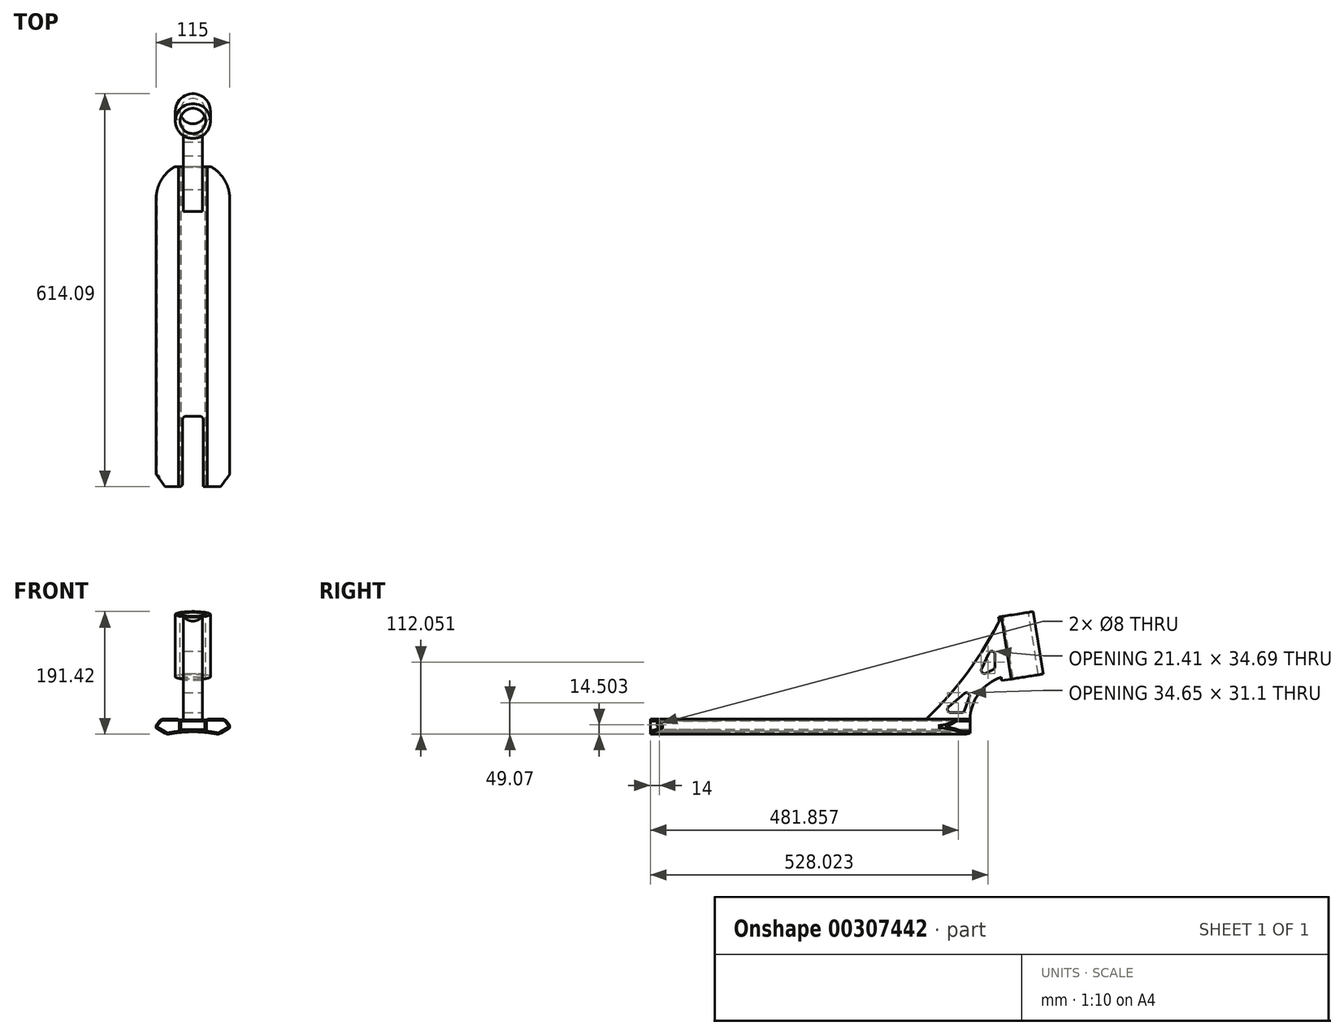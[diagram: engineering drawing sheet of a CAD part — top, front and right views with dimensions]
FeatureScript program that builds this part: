
annotation { "Feature Type Name" : "Feature", "Feature Type Description" : "" }
export const myFeature = defineFeature(function(context is Context, id is Id, definition is map)
    precondition{}
    {
        {
            var Q0;
            Q0=qCreatedBy(makeId("Front.planeOp"),FACE);
            var sketch = newSketch(context, id + "F0", { "sketchPlane" : qUnion([Q0])});
            skLineSegment(sketch, "E0", {"start": v(0, 0) * mm, "end": v(22.5, 0) * mm});
            skLineSegment(sketch, "E1", {"start": v(22.5, 0) * mm, "end": v(22.5, 1.3) * mm});
            skLineSegment(sketch, "E2", {"start": v(22.5, 1.3) * mm, "end": v(50.06, 1.3) * mm});
            skLineSegment(sketch, "E3", {"start": v(50.06, 1.3) * mm, "end": v(57.5, -8.7) * mm});
            skLineSegment(sketch, "E4", {"start": v(57.5, -8.7) * mm, "end": v(57.5, -12.7) * mm});
            skLineSegment(sketch, "E5", {"start": v(57.5, -12.7) * mm, "end": v(40.18, -22.7) * mm});
            skLineSegment(sketch, "E6.MirrorCS", {"start": v(0, 0) * mm, "end": v(-22.5, 0) * mm});
            skLineSegment(sketch, "E7.MirrorCS", {"start": v(-22.5, 0) * mm, "end": v(-22.5, 1.3) * mm});
            skLineSegment(sketch, "E8.MirrorCS", {"start": v(-22.5, 1.3) * mm, "end": v(-50.06, 1.3) * mm});
            skLineSegment(sketch, "E9.MirrorCS", {"start": v(-50.06, 1.3) * mm, "end": v(-57.5, -8.7) * mm});
            skLineSegment(sketch, "E10.MirrorCS", {"start": v(-57.5, -8.7) * mm, "end": v(-57.5, -12.7) * mm});
            skLineSegment(sketch, "E11.MirrorCS", {"start": v(-57.5, -12.7) * mm, "end": v(-40.18, -22.7) * mm});
            skArc(sketch, "E12", {"start": v(40.18, -22.7) * mm, "mid": v(0, -18.62) * mm, "end": v(-40.18, -22.7) * mm});
            skSolve(sketch);
        }
        {
            var Q0;
            Q0 = qSketchRegion(id + "F0", true);
            extrude(context, id + "F1", {"entities" : qUnion([Q0]), "endBound" : BoundingType.SYMMETRIC, "depth" : 500 * mm});
        }
        {
            var Q0;
            Q0=qCreatedBy(makeId("Front.planeOp"),FACE);
            var sketch = newSketch(context, id + "F2", { "sketchPlane" : qUnion([Q0])});
            skLineSegment(sketch, "E13.bottom", {"start": v(-19, -2) * mm, "end": v(19, -2) * mm});
            skLineSegment(sketch, "E13.top", {"start": v(-19, -15) * mm, "end": v(19, -15) * mm});
            skLineSegment(sketch, "E13.left", {"start": v(-19, -2) * mm, "end": v(-19, -15) * mm});
            skLineSegment(sketch, "E13.right", {"start": v(19, -2) * mm, "end": v(19, -15) * mm});
            skSolve(sketch);
        }
        {
            var Q0;
            Q0 = qSketchRegion(id + "F2", true);
            extrude(context, id + "F3", {"entities" : qUnion([Q0]), "operationType" : NewBodyOperationType.REMOVE, "endBound" : BoundingType.SYMMETRIC, "oppositeDirection" : true, "depth" : 500 * mm});
        }
        {
            var Q0;
            Q0=makeQuery(id+"F1.opExtrude","SWEPT_EDGE",EDGE,{"disambiguationData":[OSD([sQuery(id+"F0.wireOp",EDGE,"E7.MirrorCS"),sQuery(id+"F0.wireOp",EDGE,"E8.MirrorCS")])]});
            var Q1;
            Q1=makeQuery(id+"F1.opExtrude","SWEPT_EDGE",EDGE,{"disambiguationData":[OSD([sQuery(id+"F0.wireOp",EDGE,"E1"),sQuery(id+"F0.wireOp",EDGE,"E2")])]});
            fillet(context, id + "F4", {"entities" : qUnion([Q0, Q1]), "radius" : 2 * mm, "tangentPropagation" : true, "allowEdgeOverflow" : false});
        }
        {
            var Q0;
            Q0=makeQuery(id+"F1.opExtrude","SWEPT_EDGE",EDGE,{"disambiguationData":[OSD([sQuery(id+"F0.wireOp",EDGE,"E8.MirrorCS"),sQuery(id+"F0.wireOp",EDGE,"E9.MirrorCS")])]});
            var Q1;
            Q1=makeQuery(id+"F1.opExtrude","SWEPT_EDGE",EDGE,{"disambiguationData":[OSD([sQuery(id+"F0.wireOp",EDGE,"E11.MirrorCS"),sQuery(id+"F0.wireOp",EDGE,"E12")])]});
            var Q2;
            Q2=makeQuery(id+"F1.opExtrude","SWEPT_EDGE",EDGE,{"disambiguationData":[OSD([sQuery(id+"F0.wireOp",EDGE,"E2"),sQuery(id+"F0.wireOp",EDGE,"E3")])]});
            var Q3;
            Q3=makeQuery(id+"F1.opExtrude","SWEPT_EDGE",EDGE,{"disambiguationData":[OSD([sQuery(id+"F0.wireOp",EDGE,"E5"),sQuery(id+"F0.wireOp",EDGE,"E12")])]});
            fillet(context, id + "F5", {"entities" : qUnion([Q0, Q1, Q2, Q3]), "radius" : 9 * mm, "tangentPropagation" : true, "allowEdgeOverflow" : false});
        }
        {
            var Q0;
            Q0=makeQuery(id+"F1.opExtrude","SWEPT_EDGE",EDGE,{"disambiguationData":[OSD([sQuery(id+"F0.wireOp",EDGE,"E3"),sQuery(id+"F0.wireOp",EDGE,"E4")])]});
            var Q1;
            Q1=makeQuery(id+"F1.opExtrude","SWEPT_EDGE",EDGE,{"disambiguationData":[OSD([sQuery(id+"F0.wireOp",EDGE,"E4"),sQuery(id+"F0.wireOp",EDGE,"E5")])]});
            var Q2;
            Q2=makeQuery(id+"F1.opExtrude","SWEPT_EDGE",EDGE,{"disambiguationData":[OSD([sQuery(id+"F0.wireOp",EDGE,"E9.MirrorCS"),sQuery(id+"F0.wireOp",EDGE,"E10.MirrorCS")])]});
            var Q3;
            Q3=makeQuery(id+"F1.opExtrude","SWEPT_EDGE",EDGE,{"disambiguationData":[OSD([sQuery(id+"F0.wireOp",EDGE,"E10.MirrorCS"),sQuery(id+"F0.wireOp",EDGE,"E11.MirrorCS")])]});
            fillet(context, id + "F6", {"entities" : qUnion([Q0, Q1, Q2, Q3]), "radius" : 1 * mm, "tangentPropagation" : true, "allowEdgeOverflow" : false});
        }
        {
            var Q0;
            Q0=makeQuery(id+"F1.opExtrude","CAP_FACE",FACE,{"disambiguationData":[OSD([sQuery(id+"F0.wireOp",EDGE,"E0"),sQuery(id+"F0.wireOp",EDGE,"E1"),sQuery(id+"F0.wireOp",EDGE,"E2"),sQuery(id+"F0.wireOp",EDGE,"E3"),sQuery(id+"F0.wireOp",EDGE,"E4"),sQuery(id+"F0.wireOp",EDGE,"E5"),sQuery(id+"F0.wireOp",EDGE,"E6.MirrorCS"),sQuery(id+"F0.wireOp",EDGE,"E7.MirrorCS"),sQuery(id+"F0.wireOp",EDGE,"E8.MirrorCS"),sQuery(id+"F0.wireOp",EDGE,"E9.MirrorCS"),sQuery(id+"F0.wireOp",EDGE,"E10.MirrorCS"),sQuery(id+"F0.wireOp",EDGE,"E11.MirrorCS"),sQuery(id+"F0.wireOp",EDGE,"E12")])],"isStart":false});
            var sketch = newSketch(context, id + "F7", { "sketchPlane" : qUnion([Q0])});
            skLineSegment(sketch, "E14.0.0", {"start": v(43.1, -21.01) * mm, "end": v(57, -12.99) * mm});
            skArc(sketch, "E14.0.1", {"start": v(57, -12.99) * mm, "mid": v(57.37, -12.62) * mm, "end": v(57.5, -12.12) * mm});
            skLineSegment(sketch, "E14.0.2", {"start": v(57.5, -12.12) * mm, "end": v(57.5, -9.03) * mm});
            skArc(sketch, "E14.0.3", {"start": v(57.5, -9.03) * mm, "mid": v(57.45, -8.72) * mm, "end": v(57.3, -8.43) * mm});
            skLineSegment(sketch, "E14.0.4", {"start": v(57.3, -8.43) * mm, "end": v(52.75, -2.33) * mm});
            skArc(sketch, "E14.0.5", {"start": v(52.75, -2.33) * mm, "mid": v(49.57, 0.34) * mm, "end": v(45.54, 1.3) * mm});
            skLineSegment(sketch, "E14.0.6", {"start": v(45.54, 1.3) * mm, "end": v(24.37, 1.3) * mm});
            skArc(sketch, "E14.0.7", {"start": v(24.37, 1.3) * mm, "mid": v(23.23, 0.94) * mm, "end": v(22.5, 0) * mm});
            skLineSegment(sketch, "E14.0.8", {"start": v(22.5, 0) * mm, "end": v(-22.5, 0) * mm});
            skArc(sketch, "E14.0.9", {"start": v(-22.5, 0) * mm, "mid": v(-23.23, 0.94) * mm, "end": v(-24.37, 1.3) * mm});
            skLineSegment(sketch, "E14.0.10", {"start": v(-24.37, 1.3) * mm, "end": v(-45.54, 1.3) * mm});
            skArc(sketch, "E14.0.11", {"start": v(-45.54, 1.3) * mm, "mid": v(-49.57, 0.34) * mm, "end": v(-52.75, -2.33) * mm});
            skLineSegment(sketch, "E14.0.12", {"start": v(-52.75, -2.33) * mm, "end": v(-57.3, -8.43) * mm});
            skArc(sketch, "E14.0.13", {"start": v(-57.3, -8.43) * mm, "mid": v(-57.45, -8.72) * mm, "end": v(-57.5, -9.03) * mm});
            skLineSegment(sketch, "E14.0.14", {"start": v(-57.5, -9.03) * mm, "end": v(-57.5, -12.12) * mm});
            skArc(sketch, "E14.0.15", {"start": v(-57.5, -12.12) * mm, "mid": v(-57.37, -12.62) * mm, "end": v(-57, -12.99) * mm});
            skLineSegment(sketch, "E14.0.16", {"start": v(-57, -12.99) * mm, "end": v(-43.1, -21.01) * mm});
            skArc(sketch, "E14.0.17", {"start": v(-43.1, -21.01) * mm, "mid": v(-40.12, -22.1) * mm, "end": v(-36.94, -22.06) * mm});
            skArc(sketch, "E14.0.18", {"start": v(-36.94, -22.06) * mm, "mid": v(0, -18.62) * mm, "end": v(36.94, -22.06) * mm});
            skArc(sketch, "E14.0.19", {"start": v(36.94, -22.06) * mm, "mid": v(40.12, -22.1) * mm, "end": v(43.1, -21.01) * mm});
            skArc(sketch, "E15.0", {"start": v(-37.3, -20.1) * mm, "mid": v(0, -16.62) * mm, "end": v(37.3, -20.1) * mm});
            skArc(sketch, "E15.1", {"start": v(-42.1, -19.28) * mm, "mid": v(-39.78, -20.12) * mm, "end": v(-37.3, -20.1) * mm});
            skLineSegment(sketch, "E15.2", {"start": v(-24.37, -0.7) * mm, "end": v(-45.54, -0.7) * mm});
            skArc(sketch, "E15.3", {"start": v(-45.54, -0.7) * mm, "mid": v(-48.68, -1.44) * mm, "end": v(-51.15, -3.52) * mm});
            skLineSegment(sketch, "E15.4", {"start": v(-51.15, -3.52) * mm, "end": v(-55.97, -9.99) * mm});
            skLineSegment(sketch, "E15.5", {"start": v(-55.66, -11.45) * mm, "end": v(-42.1, -19.28) * mm});
            skArc(sketch, "E16", {"start": v(-24.37, -0.7) * mm, "mid": v(-23.23, -1.06) * mm, "end": v(-22.5, -2) * mm});
            skLineSegment(sketch, "E17", {"start": v(-22.5, -2) * mm, "end": v(-21, -2) * mm});
            skLineSegment(sketch, "E18", {"start": v(-21, -2) * mm, "end": v(-21, -17.72) * mm});
            skLineSegment(sketch, "E19", {"start": v(-56.64, -10.89) * mm, "end": v(-56.64, -10.89) * mm});
            skPoint(sketch, "E20.visualSharp", {"position": v(-56.64, -10.89) * mm});
            skArc(sketch, "E20.filletArc", {"start": v(-55.97, -9.99) * mm, "mid": v(-56.14, -10.79) * mm, "end": v(-55.66, -11.45) * mm});
            skArc(sketch, "E21.MirrorCS", {"start": v(24.37, -0.7) * mm, "mid": v(23.23, -1.06) * mm, "end": v(22.5, -2) * mm});
            skLineSegment(sketch, "E22.MirrorCS", {"start": v(22.5, -2) * mm, "end": v(21, -2) * mm});
            skLineSegment(sketch, "E23.MirrorCS", {"start": v(21, -2) * mm, "end": v(21, -17.72) * mm});
            skArc(sketch, "E24.MirrorCS", {"start": v(37.3, -20.1) * mm, "mid": v(0, -16.62) * mm, "end": v(-37.3, -20.1) * mm});
            skArc(sketch, "E25.MirrorCS", {"start": v(42.1, -19.28) * mm, "mid": v(39.78, -20.12) * mm, "end": v(37.3, -20.1) * mm});
            skLineSegment(sketch, "E26.MirrorCS", {"start": v(55.66, -11.45) * mm, "end": v(42.1, -19.28) * mm});
            skArc(sketch, "E27.MirrorCS", {"start": v(55.97, -9.99) * mm, "mid": v(56.14, -10.79) * mm, "end": v(55.66, -11.45) * mm});
            skLineSegment(sketch, "E28.MirrorCS", {"start": v(24.37, -0.7) * mm, "end": v(45.54, -0.7) * mm});
            skLineSegment(sketch, "E29.MirrorCS", {"start": v(51.15, -3.52) * mm, "end": v(55.97, -9.99) * mm});
            skArc(sketch, "E30.MirrorCS", {"start": v(45.54, -0.7) * mm, "mid": v(48.68, -1.44) * mm, "end": v(51.15, -3.52) * mm});
            skSolve(sketch);
        }
        {
            var Q0;
            {var subQ1=sQuery(id+"F7.wireOp",EDGE,"E15.1");Q0=makeQuery(id+"F7.imprint","IMPRINT",FACE,{"disambiguationData":[TD([[makeQuery(id+"F7.imprint","IMPRINT",EDGE,{"derivedFrom":subQ1}),1.0]])]});}
            var Q1;
            Q1=makeQuery(id+"F7.imprint","IMPRINT",FACE,{"disambiguationData":[TD([[makeQuery(id+"F7.imprint","IMPRINT",EDGE,{"derivedFrom":sQuery(id+"F7.wireOp",EDGE,"E21.MirrorCS")}),1.0]])]});
            extrude(context, id + "F8", {"entities" : qUnion([Q0, Q1]), "operationType" : NewBodyOperationType.REMOVE, "endBound" : BoundingType.THROUGH_ALL, "oppositeDirection" : true, "depth" : 25 * mm});
        }
        {
            var Q0;
            Q0=qCreatedBy(makeId("Top.planeOp"),FACE);
            var sketch = newSketch(context, id + "F9", { "sketchPlane" : qUnion([Q0])});
            skArc(sketch, "E31", {"start": v(57.5, 200) * mm, "mid": v(0, 257.5) * mm, "end": v(-57.5, 200) * mm});
            skLineSegment(sketch, "E32", {"start": v(57.5, 200) * mm, "end": v(57.5, 280) * mm});
            skLineSegment(sketch, "E33", {"start": v(57.5, 280) * mm, "end": v(-57.5, 280) * mm});
            skLineSegment(sketch, "E34", {"start": v(-57.5, 280) * mm, "end": v(-57.5, 200) * mm});
            skSolve(sketch);
        }
        {
            var Q0;
            Q0 = qSketchRegion(id + "F9", true);
            extrude(context, id + "F10", {"entities" : qUnion([Q0]), "operationType" : NewBodyOperationType.REMOVE, "endBound" : BoundingType.THROUGH_ALL, "oppositeDirection" : true, "depth" : 25 * mm, "hasSecondDirection" : true, "secondDirectionBound" : SecondDirectionBoundingType.THROUGH_ALL, "secondDirectionOppositeDirection" : false, "secondDirectionDepth" : 25 * mm});
        }
        {
            var Q0;
            Q0=qCreatedBy(makeId("Top.planeOp"),FACE);
            var sketch = newSketch(context, id + "F11", { "sketchPlane" : qUnion([Q0])});
            skLineSegment(sketch, "E35", {"start": v(-68, -216) * mm, "end": v(-43.3, -250) * mm});
            skLineSegment(sketch, "E36", {"start": v(-16, -250) * mm, "end": v(-16, -140) * mm});
            skLineSegment(sketch, "E37", {"start": v(-16, -140) * mm, "end": v(16, -140) * mm});
            skLineSegment(sketch, "E38", {"start": v(16, -140) * mm, "end": v(16, -250) * mm});
            skLineSegment(sketch, "E39", {"start": v(16, -250) * mm, "end": v(43.3, -250) * mm});
            skLineSegment(sketch, "E40", {"start": v(43.3, -250) * mm, "end": v(68, -216) * mm});
            skLineSegment(sketch, "E41", {"start": v(-43.3, -250) * mm, "end": v(-16, -250) * mm});
            skLineSegment(sketch, "E42", {"start": v(-68, -216) * mm, "end": v(-68, -346) * mm});
            skLineSegment(sketch, "E43", {"start": v(68, -216) * mm, "end": v(68, -346) * mm});
            skLineSegment(sketch, "E44", {"start": v(68, -346) * mm, "end": v(-68, -346) * mm});
            skSolve(sketch);
        }
        {
            var Q0;
            Q0 = qSketchRegion(id + "F11", true);
            extrude(context, id + "F12", {"entities" : qUnion([Q0]), "operationType" : NewBodyOperationType.REMOVE, "endBound" : BoundingType.THROUGH_ALL, "depth" : 25 * mm, "hasSecondDirection" : true, "secondDirectionBound" : SecondDirectionBoundingType.THROUGH_ALL, "secondDirectionOppositeDirection" : true, "secondDirectionDepth" : 25 * mm});
        }
        {
            var Q0;
            {var subQ0=sQuery(id+"F11.wireOp",EDGE,"E37");var subQ1=sQuery(id+"F11.wireOp",EDGE,"E36");Q0=makeQuery(id+"F12.boolean.opBoolean","COPY",EDGE,{"disambiguationData":[TD([makeQuery(id+"F1.opExtrude","SWEPT_FACE",FACE,{"disambiguationData":[OSD([sQuery(id+"F0.wireOp",EDGE,"E12")])]})])],"derivedFrom":makeQuery(id+"F12.opExtrude","SWEPT_EDGE",EDGE,{"disambiguationData":[OSD([subQ1,subQ0])]})});}
            var Q1;
            {var subQ0=sQuery(id+"F11.wireOp",EDGE,"E37");var subQ1=sQuery(id+"F11.wireOp",EDGE,"E38");Q1=makeQuery(id+"F12.boolean.opBoolean","COPY",EDGE,{"disambiguationData":[TD([makeQuery(id+"F3.boolean.opBoolean","COPY",FACE,{"derivedFrom":makeQuery(id+"F3.opExtrude","SWEPT_FACE",FACE,{"disambiguationData":[OSD([sQuery(id+"F2.wireOp",EDGE,"E13.bottom")])]})})])],"derivedFrom":makeQuery(id+"F12.opExtrude","SWEPT_EDGE",EDGE,{"disambiguationData":[OSD([subQ0,subQ1])]})});}
            var Q2;
            {var subQ0=sQuery(id+"F11.wireOp",EDGE,"E37");var subQ1=sQuery(id+"F11.wireOp",EDGE,"E38");Q2=makeQuery(id+"F12.boolean.opBoolean","COPY",EDGE,{"disambiguationData":[TD([makeQuery(id+"F1.opExtrude","SWEPT_FACE",FACE,{"disambiguationData":[OSD([sQuery(id+"F0.wireOp",EDGE,"E12")])]})])],"derivedFrom":makeQuery(id+"F12.opExtrude","SWEPT_EDGE",EDGE,{"disambiguationData":[OSD([subQ0,subQ1])]})});}
            var Q3;
            {var subQ0=sQuery(id+"F11.wireOp",EDGE,"E36");var subQ1=sQuery(id+"F11.wireOp",EDGE,"E37");Q3=makeQuery(id+"F12.boolean.opBoolean","COPY",EDGE,{"disambiguationData":[TD([makeQuery(id+"F3.boolean.opBoolean","COPY",FACE,{"derivedFrom":makeQuery(id+"F3.opExtrude","SWEPT_FACE",FACE,{"disambiguationData":[OSD([sQuery(id+"F2.wireOp",EDGE,"E13.bottom")])]})})])],"derivedFrom":makeQuery(id+"F12.opExtrude","SWEPT_EDGE",EDGE,{"disambiguationData":[OSD([subQ0,subQ1])]})});}
            var Q4;
            {var subQ2=sQuery(id+"F11.wireOp",EDGE,"E36");Q4=makeQuery(id+"F12.boolean.opBoolean","COPY",EDGE,{"disambiguationData":[TD([makeQuery(id+"F3.boolean.opBoolean","COPY",FACE,{"derivedFrom":makeQuery(id+"F3.opExtrude","SWEPT_FACE",FACE,{"disambiguationData":[OSD([sQuery(id+"F2.wireOp",EDGE,"E13.bottom")])]})})])],"derivedFrom":makeQuery(id+"F12.opExtrude","SWEPT_EDGE",EDGE,{"disambiguationData":[OSD([subQ2,sQuery(id+"F11.wireOp",EDGE,"E41")])]})});}
            var Q5;
            {var subQ0=sQuery(id+"F0.wireOp",EDGE,"E12");var subQ1=sQuery(id+"F11.wireOp",EDGE,"E36");Q5=makeQuery(id+"F12.boolean.opBoolean","COPY",EDGE,{"disambiguationData":[TD([makeQuery(id+"F1.opExtrude","SWEPT_FACE",FACE,{"disambiguationData":[OSD([subQ0])]})])],"derivedFrom":makeQuery(id+"F12.opExtrude","SWEPT_EDGE",EDGE,{"disambiguationData":[OSD([subQ1,sQuery(id+"F11.wireOp",EDGE,"E41")])]})});}
            var Q6;
            {var subQ2=sQuery(id+"F11.wireOp",EDGE,"E38");Q6=makeQuery(id+"F12.boolean.opBoolean","COPY",EDGE,{"disambiguationData":[TD([makeQuery(id+"F3.boolean.opBoolean","COPY",FACE,{"derivedFrom":makeQuery(id+"F3.opExtrude","SWEPT_FACE",FACE,{"disambiguationData":[OSD([sQuery(id+"F2.wireOp",EDGE,"E13.bottom")])]})})])],"derivedFrom":makeQuery(id+"F12.opExtrude","SWEPT_EDGE",EDGE,{"disambiguationData":[OSD([subQ2,sQuery(id+"F11.wireOp",EDGE,"E39")])]})});}
            var Q7;
            {var subQ0=sQuery(id+"F0.wireOp",EDGE,"E12");var subQ1=sQuery(id+"F11.wireOp",EDGE,"E38");Q7=makeQuery(id+"F12.boolean.opBoolean","COPY",EDGE,{"disambiguationData":[TD([makeQuery(id+"F1.opExtrude","SWEPT_FACE",FACE,{"disambiguationData":[OSD([subQ0])]})])],"derivedFrom":makeQuery(id+"F12.opExtrude","SWEPT_EDGE",EDGE,{"disambiguationData":[OSD([subQ1,sQuery(id+"F11.wireOp",EDGE,"E39")])]})});}
            fillet(context, id + "F13", {"entities" : qUnion([Q0, Q1, Q2, Q3, Q4, Q5, Q6, Q7]), "radius" : 5 * mm, "tangentPropagation" : true, "allowEdgeOverflow" : false});
        }
        {
            var Q0;
            Q0=qCreatedBy(makeId("Right.planeOp"),FACE);
            var sketch = newSketch(context, id + "F14", { "sketchPlane" : qUnion([Q0])});
            skLineSegment(sketch, "E45", {"start": v(180, 0) * mm, "end": v(250, 0) * mm});
            skArc(sketch, "E46", {"start": v(180, 0) * mm, "mid": v(246.79, 75.2) * mm, "end": v(298.76, 161.3) * mm});
            skLineSegment(sketch, "E47", {"start": v(298.76, 161.3) * mm, "end": v(344.2, 168.5) * mm});
            skLineSegment(sketch, "E48", {"start": v(344.2, 168.5) * mm, "end": v(344.2, 68.5) * mm});
            skArc(sketch, "E49", {"start": v(298.76, 66.7) * mm, "mid": v(263.5, 41.31) * mm, "end": v(250, 0) * mm});
            skLineSegment(sketch, "E50", {"start": v(298.76, 66.7) * mm, "end": v(298.76, 61.3) * mm});
            skLineSegment(sketch, "E51", {"start": v(298.76, 61.3) * mm, "end": v(344.2, 68.5) * mm});
            skSolve(sketch);
        }
        {
            var Q0;
            Q0 = qSketchRegion(id + "F14", true);
            extrude(context, id + "F15", {"entities" : qUnion([Q0]), "operationType" : NewBodyOperationType.ADD, "endBound" : BoundingType.SYMMETRIC, "depth" : 30 * mm});
        }
        {
            var Q0;
            Q0=makeQuery(id+"F15.opExtrude","SWEPT_FACE",FACE,{"disambiguationData":[OSD([sQuery(id+"F14.wireOp",EDGE,"E47")])]});
            var sketch = newSketch(context, id + "F16", { "sketchPlane" : qUnion([Q0])});
            skCircle(sketch, "E52", {"center": v(0, 343.32) * mm, "radius": 27.5 * mm});
            skSolve(sketch);
        }
        {
            var Q0;
            Q0 = qSketchRegion(id + "F16", true);
            var Q1;
            Q1=makeQuery(id+"F15.opExtrude","SWEPT_FACE",FACE,{"disambiguationData":[OSD([sQuery(id+"F14.wireOp",EDGE,"E51")])]});
            extrude(context, id + "F17", {"entities" : qUnion([Q0]), "operationType" : NewBodyOperationType.ADD, "endBound" : BoundingType.UP_TO_SURFACE, "oppositeDirection" : true, "endBoundEntityFace" : qUnion([Q1]), "depth" : 25 * mm});
        }
        {
            var Q0;
            Q0=makeQuery(id+"F17.boolean.opBoolean","MERGE",FACE,{"derivedFrom":[makeQuery(id+"F15.opExtrude","SWEPT_FACE",FACE,{"disambiguationData":[OSD([sQuery(id+"F14.wireOp",EDGE,"E47")])]}),makeQuery(id+"F17.opExtrude","CAP_FACE",FACE,{"disambiguationData":[OSD([sQuery(id+"F16.wireOp",EDGE,"E52")])],"isStart":true})]});
            var sketch = newSketch(context, id + "F18", { "sketchPlane" : qUnion([Q0])});
            skPoint(sketch, "E53", {"position": v(0, 343.32) * mm});
            skSolve(sketch);
        }
        {
            var Q0;
            Q0=sQuery(id+"F18.wireOp",VERTEX,"E53");
            var Q1;
            Q1=makeQuery(id+"F1.opExtrude","SWEPT_BODY",BODY,{"disambiguationData":[OSD([sQuery(id+"F0.wireOp",EDGE,"E0"),sQuery(id+"F0.wireOp",EDGE,"E1"),sQuery(id+"F0.wireOp",EDGE,"E2"),sQuery(id+"F0.wireOp",EDGE,"E3"),sQuery(id+"F0.wireOp",EDGE,"E4"),sQuery(id+"F0.wireOp",EDGE,"E5"),sQuery(id+"F0.wireOp",EDGE,"E6.MirrorCS"),sQuery(id+"F0.wireOp",EDGE,"E7.MirrorCS"),sQuery(id+"F0.wireOp",EDGE,"E8.MirrorCS"),sQuery(id+"F0.wireOp",EDGE,"E9.MirrorCS"),sQuery(id+"F0.wireOp",EDGE,"E10.MirrorCS"),sQuery(id+"F0.wireOp",EDGE,"E11.MirrorCS"),sQuery(id+"F0.wireOp",EDGE,"E12")])]});
            hole(context, id + "F19", {"style" : HoleStyle.SIMPLE, "endStyle" : HoleEndStyle.THROUGH, "holeDiameter" : 40 * mm, "isTappedThrough" : true, "tappedDepth" : 12 * mm, "tapClearance" : 3, "locations" : qUnion([Q0]), "scope" : qUnion([Q1])});
        }
        {
            var Q0;
            Q0=makeQuery(id+"F8.boolean.opBoolean","COPY",FACE,{"derivedFrom":makeQuery(id+"F8.opExtrude","SWEPT_FACE",FACE,{"disambiguationData":[OSD([sQuery(id+"F7.wireOp",EDGE,"E23.MirrorCS")])]})});
            var sketch = newSketch(context, id + "F20", { "sketchPlane" : qUnion([Q0])});
            skPoint(sketch, "E54", {"position": v(-236, -7.72) * mm});
            skPoint(sketch, "E54.positionSnap0", {"position": v(-264.37, -7.72) * mm});
            skSolve(sketch);
        }
        {
            var Q0;
            Q0=sQuery(id+"F20.wireOp",VERTEX,"E54");
            var Q1;
            Q1=makeQuery(id+"F1.opExtrude","SWEPT_BODY",BODY,{"disambiguationData":[OSD([sQuery(id+"F0.wireOp",EDGE,"E0"),sQuery(id+"F0.wireOp",EDGE,"E1"),sQuery(id+"F0.wireOp",EDGE,"E2"),sQuery(id+"F0.wireOp",EDGE,"E3"),sQuery(id+"F0.wireOp",EDGE,"E4"),sQuery(id+"F0.wireOp",EDGE,"E5"),sQuery(id+"F0.wireOp",EDGE,"E6.MirrorCS"),sQuery(id+"F0.wireOp",EDGE,"E7.MirrorCS"),sQuery(id+"F0.wireOp",EDGE,"E8.MirrorCS"),sQuery(id+"F0.wireOp",EDGE,"E9.MirrorCS"),sQuery(id+"F0.wireOp",EDGE,"E10.MirrorCS"),sQuery(id+"F0.wireOp",EDGE,"E11.MirrorCS"),sQuery(id+"F0.wireOp",EDGE,"E12")])]});
            hole(context, id + "F21", {"style" : HoleStyle.SIMPLE, "endStyle" : HoleEndStyle.THROUGH, "holeDiameter" : 8 * mm, "isTappedThrough" : true, "tappedDepth" : 12 * mm, "tapClearance" : 3, "locations" : qUnion([Q0]), "scope" : qUnion([Q1])});
        }
        {
            var Q0;
            Q0=makeQuery(id+"F15.opExtrude","CAP_FACE",FACE,{"disambiguationData":[OSD([sQuery(id+"F14.wireOp",EDGE,"E45"),sQuery(id+"F14.wireOp",EDGE,"E46"),sQuery(id+"F14.wireOp",EDGE,"E47"),sQuery(id+"F14.wireOp",EDGE,"E48"),sQuery(id+"F14.wireOp",EDGE,"E49"),sQuery(id+"F14.wireOp",EDGE,"E50"),sQuery(id+"F14.wireOp",EDGE,"E51")])],"isStart":false});
            var sketch = newSketch(context, id + "F22", { "sketchPlane" : qUnion([Q0])});
            skLineSegment(sketch, "E55", {"start": v(206, 11.3) * mm, "end": v(240, 11.3) * mm});
            skLineSegment(sketch, "E56", {"start": v(240, 11.3) * mm, "end": v(255.4, 53.59) * mm});
            skLineSegment(sketch, "E57", {"start": v(206, 11.3) * mm, "end": v(255.4, 53.59) * mm});
            skLineSegment(sketch, "E58", {"start": v(288.73, 124.96) * mm, "end": v(288.73, 79.96) * mm});
            skLineSegment(sketch, "E59", {"start": v(288.73, 79.96) * mm, "end": v(261.82, 66.7) * mm});
            skLineSegment(sketch, "E60", {"start": v(288.73, 124.96) * mm, "end": v(261.82, 66.7) * mm});
            skSolve(sketch);
        }
        {
            var Q0;
            Q0 = qSketchRegion(id + "F22", true);
            extrude(context, id + "F23", {"entities" : qUnion([Q0]), "operationType" : NewBodyOperationType.REMOVE, "endBound" : BoundingType.THROUGH_ALL, "oppositeDirection" : true, "depth" : 25 * mm});
        }
        {
            var Q0;
            Q0=makeQuery(id+"F23.boolean.opBoolean","COPY",EDGE,{"derivedFrom":makeQuery(id+"F23.opExtrude","SWEPT_EDGE",EDGE,{"disambiguationData":[OSD([sQuery(id+"F22.wireOp",EDGE,"E58"),sQuery(id+"F22.wireOp",EDGE,"E59")])]})});
            var Q1;
            Q1=makeQuery(id+"F23.boolean.opBoolean","COPY",EDGE,{"derivedFrom":makeQuery(id+"F23.opExtrude","SWEPT_EDGE",EDGE,{"disambiguationData":[OSD([sQuery(id+"F22.wireOp",EDGE,"E59"),sQuery(id+"F22.wireOp",EDGE,"E60")])]})});
            var Q2;
            Q2=makeQuery(id+"F23.boolean.opBoolean","COPY",EDGE,{"derivedFrom":makeQuery(id+"F23.opExtrude","SWEPT_EDGE",EDGE,{"disambiguationData":[OSD([sQuery(id+"F22.wireOp",EDGE,"E58"),sQuery(id+"F22.wireOp",EDGE,"E60")])]})});
            var Q3;
            Q3=makeQuery(id+"F23.boolean.opBoolean","COPY",EDGE,{"derivedFrom":makeQuery(id+"F23.opExtrude","SWEPT_EDGE",EDGE,{"disambiguationData":[OSD([sQuery(id+"F22.wireOp",EDGE,"E56"),sQuery(id+"F22.wireOp",EDGE,"E57")])]})});
            var Q4;
            Q4=makeQuery(id+"F23.boolean.opBoolean","COPY",EDGE,{"derivedFrom":makeQuery(id+"F23.opExtrude","SWEPT_EDGE",EDGE,{"disambiguationData":[OSD([sQuery(id+"F22.wireOp",EDGE,"E55"),sQuery(id+"F22.wireOp",EDGE,"E56")])]})});
            var Q5;
            Q5=makeQuery(id+"F23.boolean.opBoolean","COPY",EDGE,{"derivedFrom":makeQuery(id+"F23.opExtrude","SWEPT_EDGE",EDGE,{"disambiguationData":[OSD([sQuery(id+"F22.wireOp",EDGE,"E55"),sQuery(id+"F22.wireOp",EDGE,"E57")])]})});
            fillet(context, id + "F24", {"entities" : qUnion([Q0, Q1, Q2, Q3, Q4, Q5]), "radius" : 5 * mm, "tangentPropagation" : true, "allowEdgeOverflow" : false});
        }
    });
